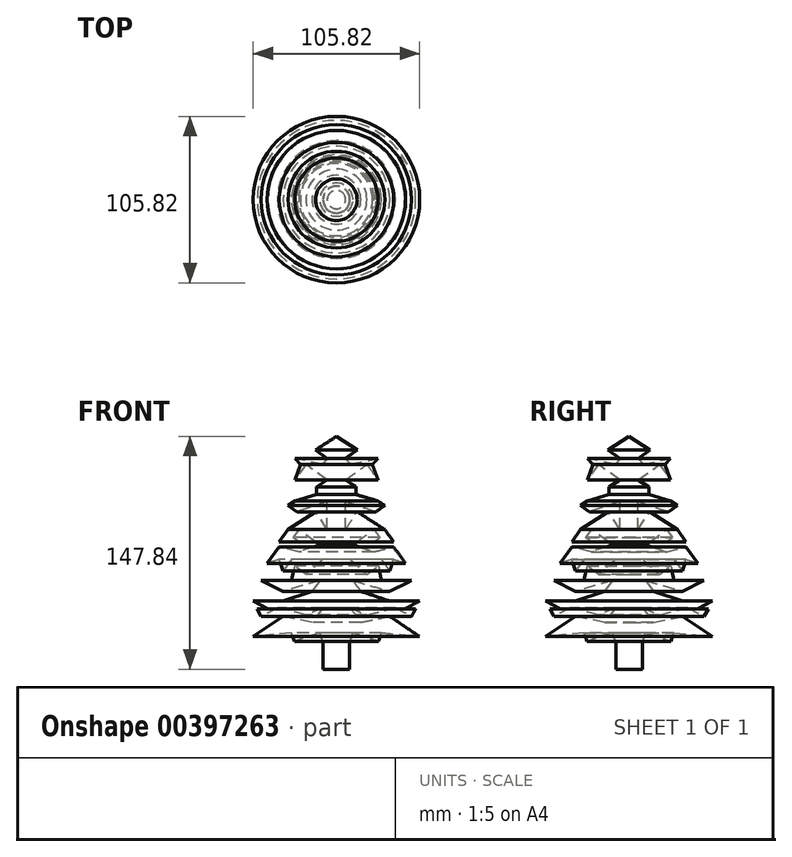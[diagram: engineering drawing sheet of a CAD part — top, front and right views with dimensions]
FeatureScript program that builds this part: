
annotation { "Feature Type Name" : "Feature", "Feature Type Description" : "" }
export const myFeature = defineFeature(function(context is Context, id is Id, definition is map)
    precondition{}
    {
        {
            var Q0;
            Q0=qCreatedBy(makeId("Front.planeOp"),FACE);
            var sketch = newSketch(context, id + "F0", { "sketchPlane" : qUnion([Q0])});
            skLineSegment(sketch, "E0", {"start": v(0, 55.81) * mm, "end": v(0, -62.91) * mm});
            skLineSegment(sketch, "E1", {"start": v(0, -62.91) * mm, "end": v(-8.71, -65.81) * mm});
            skLineSegment(sketch, "E2", {"start": v(-8.71, -65.81) * mm, "end": v(-10.52, -60.4) * mm});
            skLineSegment(sketch, "E3", {"start": v(-10.52, -60.4) * mm, "end": v(-26.78, -65.81) * mm});
            skLineSegment(sketch, "E4", {"start": v(-26.78, -65.81) * mm, "end": v(-28.58, -60.4) * mm});
            skLineSegment(sketch, "E5", {"start": v(-28.58, -60.4) * mm, "end": v(-52.9, -62.91) * mm});
            skLineSegment(sketch, "E6", {"start": v(-52.9, -62.91) * mm, "end": v(-33.88, -50) * mm});
            skLineSegment(sketch, "E7", {"start": v(-33.88, -50) * mm, "end": v(-15.49, -53.88) * mm});
            skLineSegment(sketch, "E8", {"start": v(-15.49, -53.88) * mm, "end": v(-8.71, -44.52) * mm});
            skLineSegment(sketch, "E9", {"start": v(-8.71, -44.52) * mm, "end": v(-19.36, -49.2) * mm});
            skPoint(sketch, "E9.endSnap0", {"position": v(-12.1, -49.2) * mm});
            skLineSegment(sketch, "E10", {"start": v(-19.36, -49.2) * mm, "end": v(-37.42, -44.52) * mm});
            skLineSegment(sketch, "E11", {"start": v(-37.42, -44.52) * mm, "end": v(-47.75, -50) * mm});
            skLineSegment(sketch, "E12", {"start": v(-47.75, -50) * mm, "end": v(-50.33, -45.15) * mm});
            skLineSegment(sketch, "E13", {"start": v(-52.9, -40.29) * mm, "end": v(-33.88, -40.29) * mm});
            skLineSegment(sketch, "E14", {"start": v(-33.88, -40.29) * mm, "end": v(-15.49, -34.16) * mm});
            skLineSegment(sketch, "E15", {"start": v(-15.49, -34.16) * mm, "end": v(-10.52, -27.3) * mm});
            skLineSegment(sketch, "E16", {"start": v(-10.52, -27.3) * mm, "end": v(-33.88, -34.16) * mm});
            skLineSegment(sketch, "E17", {"start": v(-33.88, -34.16) * mm, "end": v(-47.75, -27.3) * mm});
            skLineSegment(sketch, "E18", {"start": v(-47.75, -27.3) * mm, "end": v(-28.58, -27.3) * mm});
            skLineSegment(sketch, "E19", {"start": v(-28.58, -27.3) * mm, "end": v(-26.78, -18.07) * mm});
            skLineSegment(sketch, "E20", {"start": v(-26.78, -18.07) * mm, "end": v(-19.36, -23.44) * mm});
            skLineSegment(sketch, "E21", {"start": v(-19.36, -23.44) * mm, "end": v(-8.71, -13.87) * mm});
            skLineSegment(sketch, "E22", {"start": v(-8.71, -13.87) * mm, "end": v(-28.58, -13.87) * mm});
            skLineSegment(sketch, "E23", {"start": v(-28.58, -13.87) * mm, "end": v(-33.88, -21.18) * mm});
            skLineSegment(sketch, "E24", {"start": v(-33.88, -21.18) * mm, "end": v(-36.31, -13.87) * mm});
            skLineSegment(sketch, "E25", {"start": v(-36.31, -13.87) * mm, "end": v(-44, -16.43) * mm});
            skLineSegment(sketch, "E26", {"start": v(-44.2, -16.78) * mm, "end": v(-36.31, -5.88) * mm});
            skLineSegment(sketch, "E27", {"start": v(-36.31, -5.88) * mm, "end": v(-23.87, -9.03) * mm});
            skLineSegment(sketch, "E28", {"start": v(-23.87, -9.03) * mm, "end": v(-10.52, -4.58) * mm});
            skLineSegment(sketch, "E29", {"start": v(-10.52, -4.58) * mm, "end": v(-15.49, -0.98) * mm});
            skLineSegment(sketch, "E30", {"start": v(-15.49, -0.98) * mm, "end": v(-23.87, 5.1) * mm});
            skLineSegment(sketch, "E31", {"start": v(-23.87, 5.1) * mm, "end": v(-27.56, 0) * mm});
            skLineSegment(sketch, "E32", {"start": v(-27.56, 0) * mm, "end": v(-23.87, -2.67) * mm});
            skLineSegment(sketch, "E33", {"start": v(-23.87, -2.67) * mm, "end": v(-36.31, -2.67) * mm});
            skLineSegment(sketch, "E34", {"start": v(-36.31, -2.67) * mm, "end": v(-30.7, 5.1) * mm});
            skLineSegment(sketch, "E35", {"start": v(-30.7, 5.1) * mm, "end": v(-13.23, 16.45) * mm});
            skLineSegment(sketch, "E36", {"start": v(-13.23, 16.45) * mm, "end": v(-5.83, 5.1) * mm});
            skLineSegment(sketch, "E37", {"start": v(-5.83, 5.1) * mm, "end": v(-5.83, 22.9) * mm});
            skLineSegment(sketch, "E38", {"start": v(-5.83, 22.9) * mm, "end": v(-25.2, 16.45) * mm});
            skLineSegment(sketch, "E39", {"start": v(-25.2, 16.45) * mm, "end": v(-30.7, 20.44) * mm});
            skLineSegment(sketch, "E40", {"start": v(-30.7, 20.44) * mm, "end": v(-26.45, 23.2) * mm});
            skLineSegment(sketch, "E41", {"start": v(-5.83, 36.6) * mm, "end": v(-19.36, 46.4) * mm});
            skLineSegment(sketch, "E42", {"start": v(-19.36, 46.4) * mm, "end": v(-26.45, 36.6) * mm});
            skLineSegment(sketch, "E43", {"start": v(-26.45, 50.33) * mm, "end": v(-8.71, 46.4) * mm});
            skLineSegment(sketch, "E44", {"start": v(-8.71, 46.4) * mm, "end": v(-5.87, 50.33) * mm});
            skLineSegment(sketch, "E45", {"start": v(-5.87, 50.33) * mm, "end": v(-13.23, 55.66) * mm});
            skLineSegment(sketch, "E46", {"start": v(-13.23, 55.66) * mm, "end": v(0, 64.27) * mm});
            skLineSegment(sketch, "E47", {"start": v(0, 64.27) * mm, "end": v(0, 55.81) * mm});
            skLineSegment(sketch, "E48", {"start": v(-26.45, 50.33) * mm, "end": v(-22.9, 46.4) * mm});
            skPoint(sketch, "E48.endSnap0", {"position": v(-22.9, 41.5) * mm});
            skLineSegment(sketch, "E49", {"start": v(-22.9, 46.4) * mm, "end": v(-26.45, 36.6) * mm});
            skLineSegment(sketch, "E50", {"start": v(-26.45, 23.2) * mm, "end": v(-12.58, 27.32) * mm});
            skLineSegment(sketch, "E51", {"start": v(-12.58, 27.32) * mm, "end": v(-12.58, 32.22) * mm});
            skLineSegment(sketch, "E52.trimOffspring", {"start": v(-12.58, 32.22) * mm, "end": v(-5.83, 36.6) * mm});
            skLineSegment(sketch, "E53", {"start": v(-52.9, -40.29) * mm, "end": v(-43.4, -45.15) * mm});
            skPoint(sketch, "E53.endSnap0", {"position": v(-50.33, -45.15) * mm});
            skPoint(sketch, "E53.endSnap1", {"position": v(-43.4, -56.46) * mm});
            skLineSegment(sketch, "E54", {"start": v(-43.4, -45.15) * mm, "end": v(-50.33, -45.15) * mm});
            skSolve(sketch);
        }
        {
            var Q0;
            Q0 = qSketchRegion(id + "F0", true);
            var Q1;
            Q1=sQuery(id+"F0.wireOp",EDGE,"E0");
            revolve(context, id + "F1", {"entities" : qUnion([Q0]), "axis" : qUnion([Q1]), "revolveType" : RevolveType.FULL});
        }
        {
            var Q0;
            Q0=qCreatedBy(makeId("Top.planeOp"),FACE);
            var sketch = newSketch(context, id + "F2", { "sketchPlane" : qUnion([Q0])});
            skCircle(sketch, "E55", {"center": v(0, 0) * mm, "radius": 8.4 * mm});
            skSolve(sketch);
        }
        {
            var Q0;
            Q0 = qSketchRegion(id + "F2", true);
            extrude(context, id + "F3", {"entities" : qUnion([Q0]), "operationType" : NewBodyOperationType.ADD, "oppositeDirection" : true, "depth" : 83.57 * mm});
        }
    });
